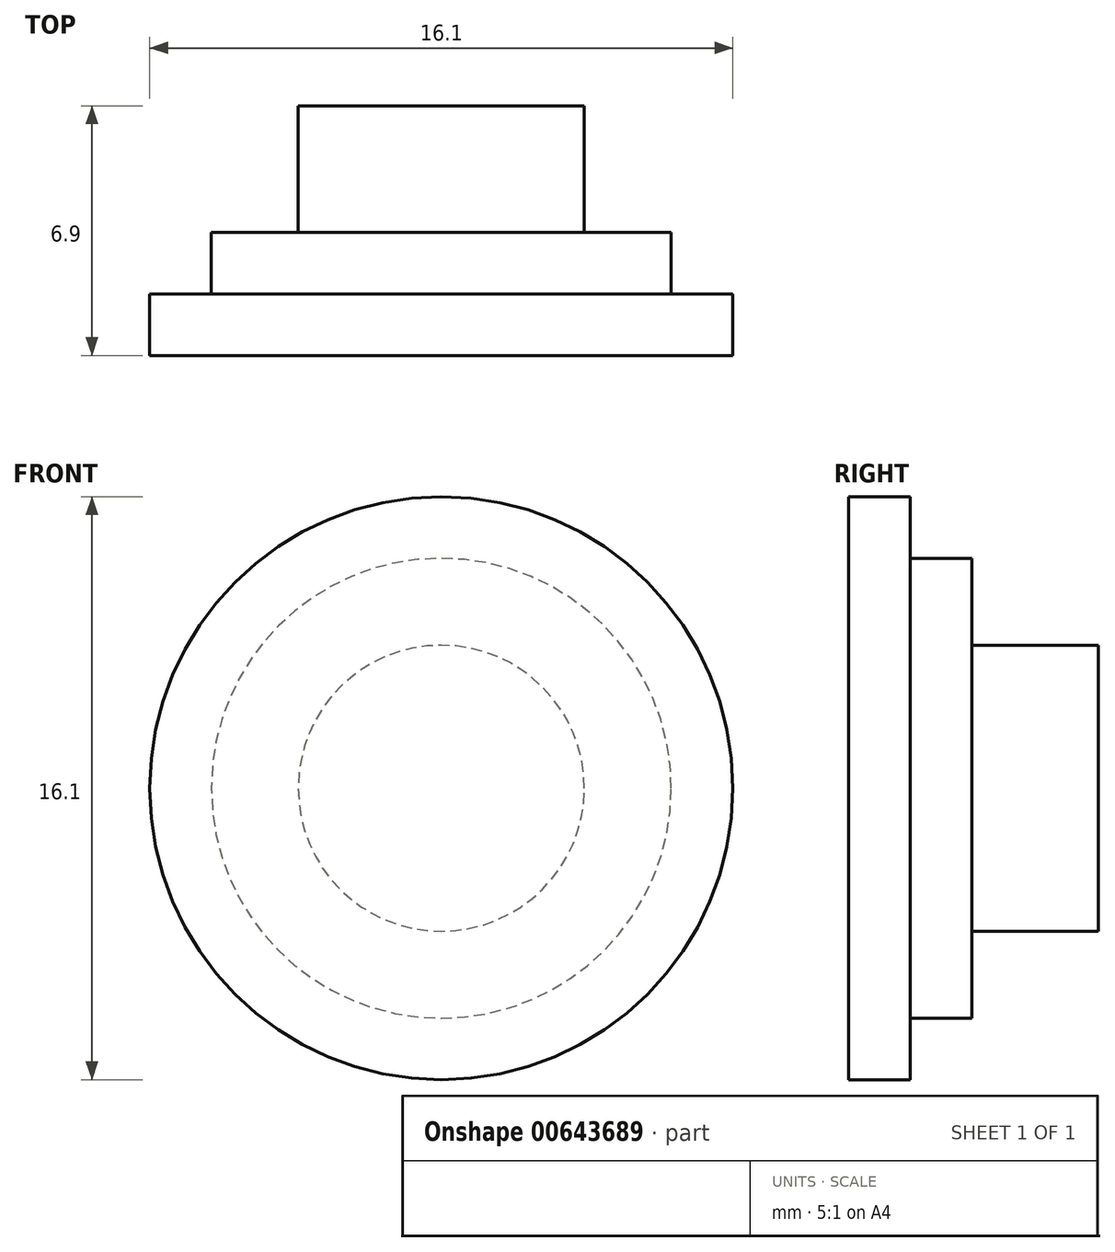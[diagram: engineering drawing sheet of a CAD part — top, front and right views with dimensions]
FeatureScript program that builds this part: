
annotation { "Feature Type Name" : "Feature", "Feature Type Description" : "" }
export const myFeature = defineFeature(function(context is Context, id is Id, definition is map)
    precondition{}
    {
        {
            var Q0;
            Q0=qCreatedBy(makeId("Right.planeOp"),FACE);
            var sketch = newSketch(context, id + "F0", { "sketchPlane" : qUnion([Q0])});
            skLineSegment(sketch, "E0", {"start": v(-56.86, 0) * mm, "end": v(48.64, 0) * mm, "construction": true});
            skLineSegment(sketch, "E1", {"start": v(12.94, 0) * mm, "end": v(12.94, 3.95) * mm});
            skLineSegment(sketch, "E2", {"start": v(12.94, 3.95) * mm, "end": v(9.44, 3.95) * mm});
            skLineSegment(sketch, "E3", {"start": v(9.44, 3.95) * mm, "end": v(9.44, 6.35) * mm});
            skLineSegment(sketch, "E4", {"start": v(9.44, 6.35) * mm, "end": v(7.74, 6.35) * mm});
            skLineSegment(sketch, "E5", {"start": v(12.94, 0) * mm, "end": v(6.04, 0) * mm});
            skPoint(sketch, "E6.endSnap0", {"position": v(9.44, 5.15) * mm});
            skLineSegment(sketch, "E7", {"start": v(7.74, 6.35) * mm, "end": v(7.74, 8.05) * mm});
            skLineSegment(sketch, "E8", {"start": v(7.74, 8.05) * mm, "end": v(6.04, 8.05) * mm});
            skLineSegment(sketch, "E9", {"start": v(6.04, 8.05) * mm, "end": v(6.04, 6.35) * mm});
            skPoint(sketch, "E9.endSnap0", {"position": v(8.59, 6.35) * mm});
            skLineSegment(sketch, "E10", {"start": v(6.04, 6.35) * mm, "end": v(6.04, 0) * mm});
            skSolve(sketch);
        }
        {
            var Q0;
            Q0 = qSketchRegion(id + "F0", true);
            var Q1;
            Q1=sQuery(id+"F0.wireOp",EDGE,"E0");
            revolve(context, id + "F1", {"entities" : qUnion([Q0]), "axis" : qUnion([Q1]), "revolveType" : RevolveType.FULL});
        }
    });
